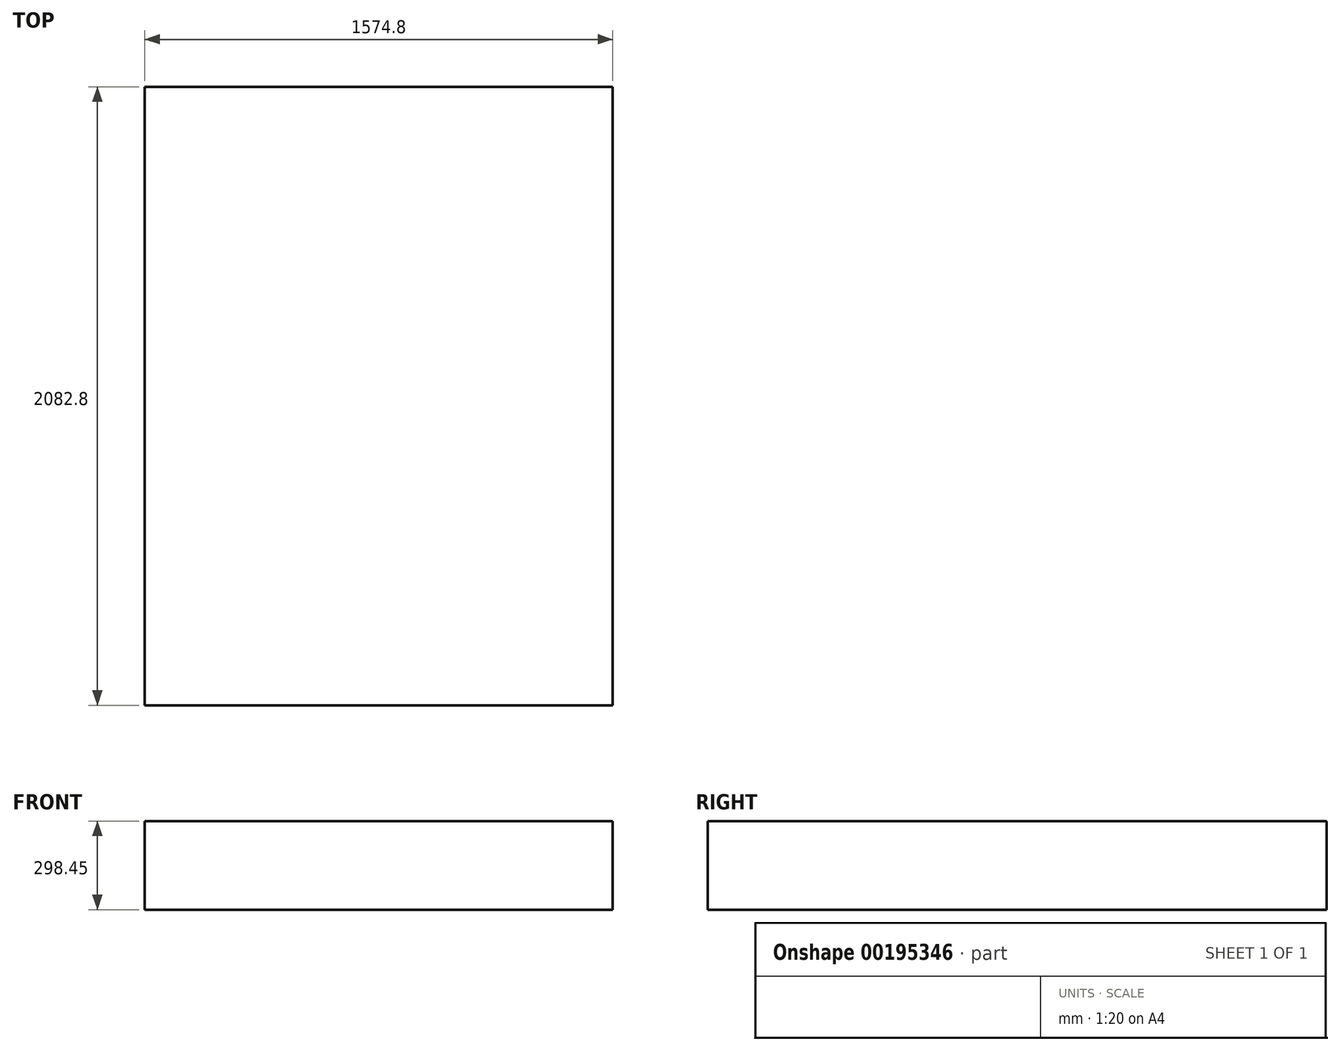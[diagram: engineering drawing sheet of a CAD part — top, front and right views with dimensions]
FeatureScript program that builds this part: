
annotation { "Feature Type Name" : "Feature", "Feature Type Description" : "" }
export const myFeature = defineFeature(function(context is Context, id is Id, definition is map)
    precondition{}
    {
        {
            var Q0;
            Q0=qCreatedBy(makeId("Top.planeOp"),FACE);
            var sketch = newSketch(context, id + "F0", { "sketchPlane" : qUnion([Q0])});
            skLineSegment(sketch, "E0.bottom", {"start": v(787.4, -1041.4) * mm, "end": v(-787.4, -1041.4) * mm});
            skLineSegment(sketch, "E0.top", {"start": v(787.4, 1041.4) * mm, "end": v(-787.4, 1041.4) * mm});
            skLineSegment(sketch, "E0.left", {"start": v(787.4, -1041.4) * mm, "end": v(787.4, 1041.4) * mm});
            skLineSegment(sketch, "E0.right", {"start": v(-787.4, -1041.4) * mm, "end": v(-787.4, 1041.4) * mm});
            skPoint(sketch, "E0.middle", {"position": v(0, 0) * mm});
            skSolve(sketch);
        }
        {
            var Q0;
            Q0=makeQuery(id+"F0.imprint","IMPRINT",FACE,{"disambiguationData":[TD([[makeQuery(id+"F0.imprint","IMPRINT",EDGE,{"derivedFrom":sQuery(id+"F0.wireOp",EDGE,"E0.bottom")}),-1.0]])]});
            extrude(context, id + "F1", {"entities" : qUnion([Q0]), "depth" : 298.45 * mm});
        }
    });
